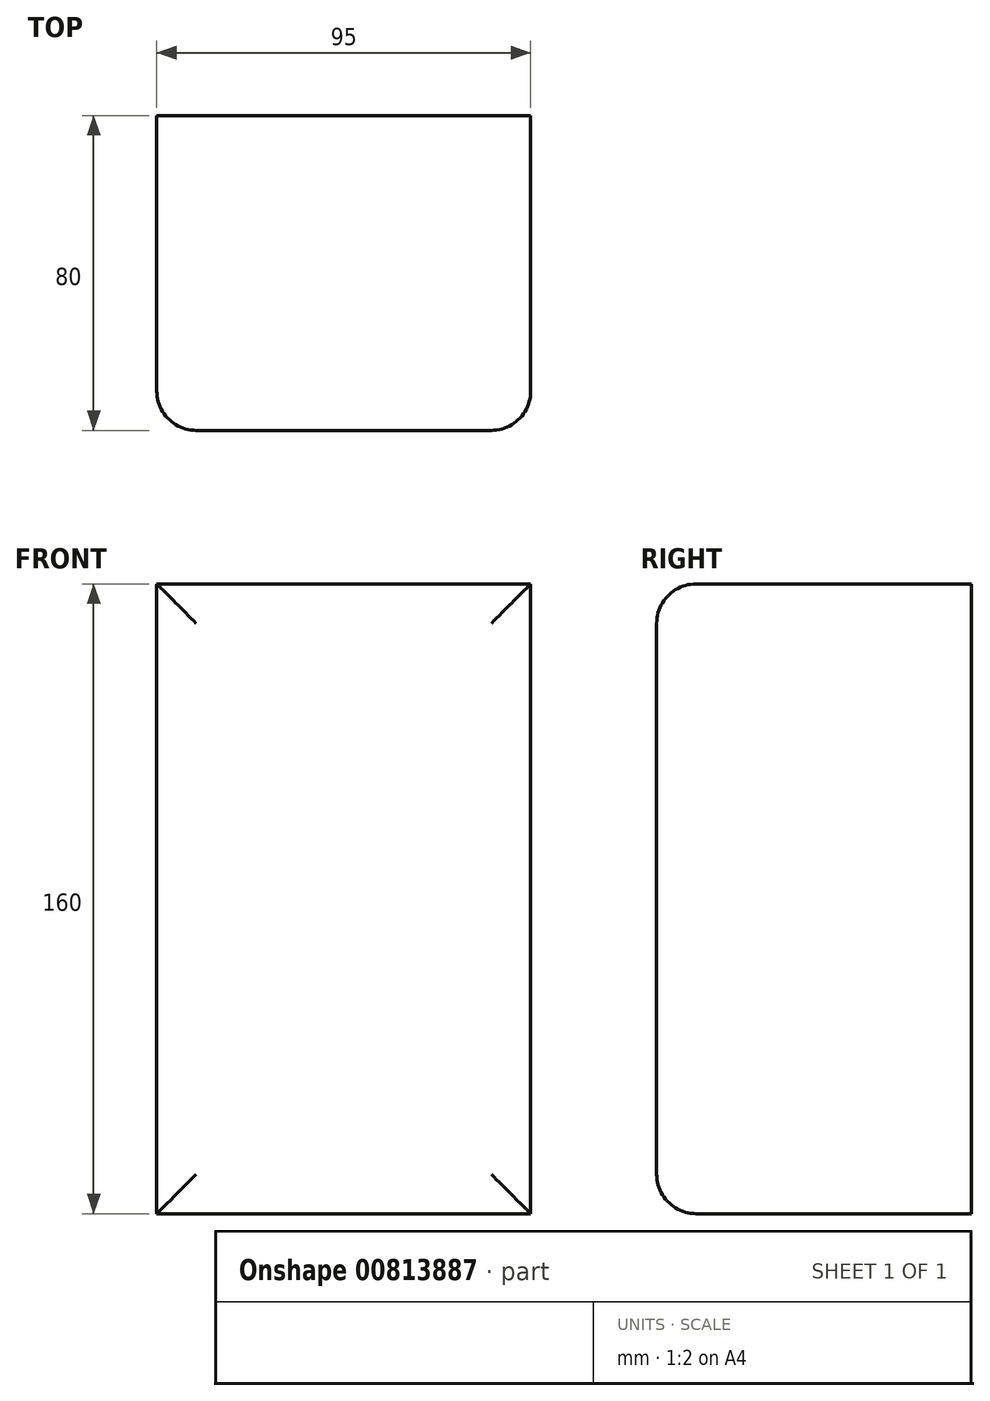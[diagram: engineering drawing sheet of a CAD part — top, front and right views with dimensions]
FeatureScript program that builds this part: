
annotation { "Feature Type Name" : "Feature", "Feature Type Description" : "" }
export const myFeature = defineFeature(function(context is Context, id is Id, definition is map)
    precondition{}
    {
        {
            var Q0;
            Q0=qCreatedBy(makeId("Front.planeOp"),FACE);
            var sketch = newSketch(context, id + "F0", { "sketchPlane" : qUnion([Q0])});
            skLineSegment(sketch, "E0.bottom", {"start": v(47.5, -80) * mm, "end": v(-47.5, -80) * mm});
            skLineSegment(sketch, "E0.top", {"start": v(47.5, 80) * mm, "end": v(-47.5, 80) * mm});
            skLineSegment(sketch, "E0.left", {"start": v(47.5, -80) * mm, "end": v(47.5, 80) * mm});
            skLineSegment(sketch, "E0.right", {"start": v(-47.5, -80) * mm, "end": v(-47.5, 80) * mm});
            skPoint(sketch, "E0.middle", {"position": v(0, 0) * mm});
            skSolve(sketch);
        }
        {
            var Q0;
            Q0 = qSketchRegion(id + "F0", true);
            extrude(context, id + "F1", {"entities" : qUnion([Q0]), "depth" : 80 * mm, "offsetDistance" : 25.4 * mm});
        }
        {
            var Q0;
            Q0=makeQuery(id+"F1.opExtrude","CAP_EDGE",EDGE,{"disambiguationData":[OSD([sQuery(id+"F0.wireOp",EDGE,"E0.top")])],"isStart":false});
            var Q1;
            Q1=makeQuery(id+"F1.opExtrude","CAP_EDGE",EDGE,{"disambiguationData":[OSD([sQuery(id+"F0.wireOp",EDGE,"E0.right")])],"isStart":false});
            var Q2;
            Q2=makeQuery(id+"F1.opExtrude","CAP_EDGE",EDGE,{"disambiguationData":[OSD([sQuery(id+"F0.wireOp",EDGE,"E0.left")])],"isStart":false});
            var Q3;
            Q3=makeQuery(id+"F1.opExtrude","CAP_EDGE",EDGE,{"disambiguationData":[OSD([sQuery(id+"F0.wireOp",EDGE,"E0.bottom")])],"isStart":false});
            fillet(context, id + "F2", {"entities" : qUnion([Q0, Q1, Q2, Q3]), "radius" : 10 * mm, "tangentPropagation" : true, "allowEdgeOverflow" : false});
        }
    });
